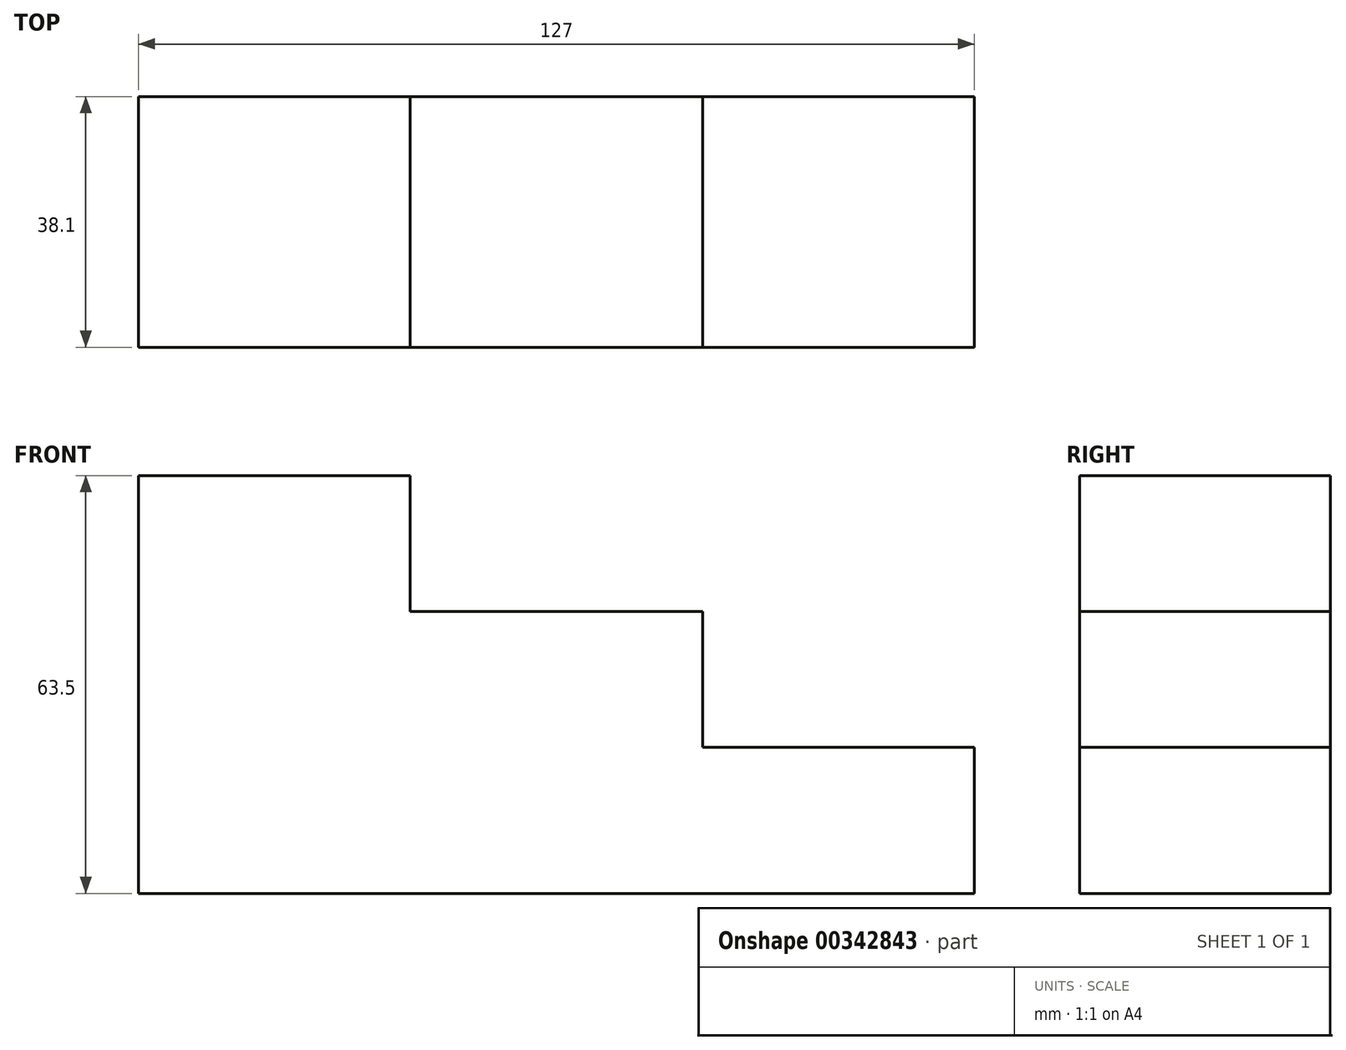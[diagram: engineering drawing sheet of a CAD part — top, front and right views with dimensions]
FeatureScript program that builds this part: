
annotation { "Feature Type Name" : "Feature", "Feature Type Description" : "" }
export const myFeature = defineFeature(function(context is Context, id is Id, definition is map)
    precondition{}
    {
        {
            var Q0;
            Q0=qCreatedBy(makeId("Front.planeOp"),FACE);
            var sketch = newSketch(context, id + "F0", { "sketchPlane" : qUnion([Q0])});
            skLineSegment(sketch, "E0.bottom", {"start": v(-63.5, -31.75) * mm, "end": v(63.5, -31.75) * mm});
            skLineSegment(sketch, "E0.top", {"start": v(-63.5, 31.75) * mm, "end": v(-22.23, 31.75) * mm});
            skLineSegment(sketch, "E0.left", {"start": v(-63.5, -31.75) * mm, "end": v(-63.5, 31.75) * mm});
            skLineSegment(sketch, "E0.right", {"start": v(63.5, -31.75) * mm, "end": v(63.5, -9.55) * mm});
            skPoint(sketch, "E0.middle", {"position": v(0, 0) * mm});
            skLineSegment(sketch, "E1", {"start": v(-22.23, 31.75) * mm, "end": v(-22.23, 11.1) * mm});
            skLineSegment(sketch, "E2", {"start": v(-22.23, 11.1) * mm, "end": v(22.22, 11.1) * mm});
            skLineSegment(sketch, "E3", {"start": v(22.22, 11.1) * mm, "end": v(22.22, -9.55) * mm});
            skLineSegment(sketch, "E4", {"start": v(22.22, -9.55) * mm, "end": v(63.5, -9.55) * mm});
            skPoint(sketch, "E5.end.orphan", {"position": v(22.22, 31.75) * mm});
            skPoint(sketch, "E6.trimOffspring.end.orphan", {"position": v(63.5, 31.75) * mm});
            skSolve(sketch);
        }
        {
            var Q0;
            Q0=makeQuery(id+"F0.imprint","IMPRINT",FACE,{"disambiguationData":[TD([[makeQuery(id+"F0.imprint","IMPRINT",EDGE,{"derivedFrom":sQuery(id+"F0.wireOp",EDGE,"E0.bottom")}),1.0]])]});
            extrude(context, id + "F1", {"entities" : qUnion([Q0]), "depth" : 38.1 * mm});
        }
    });
